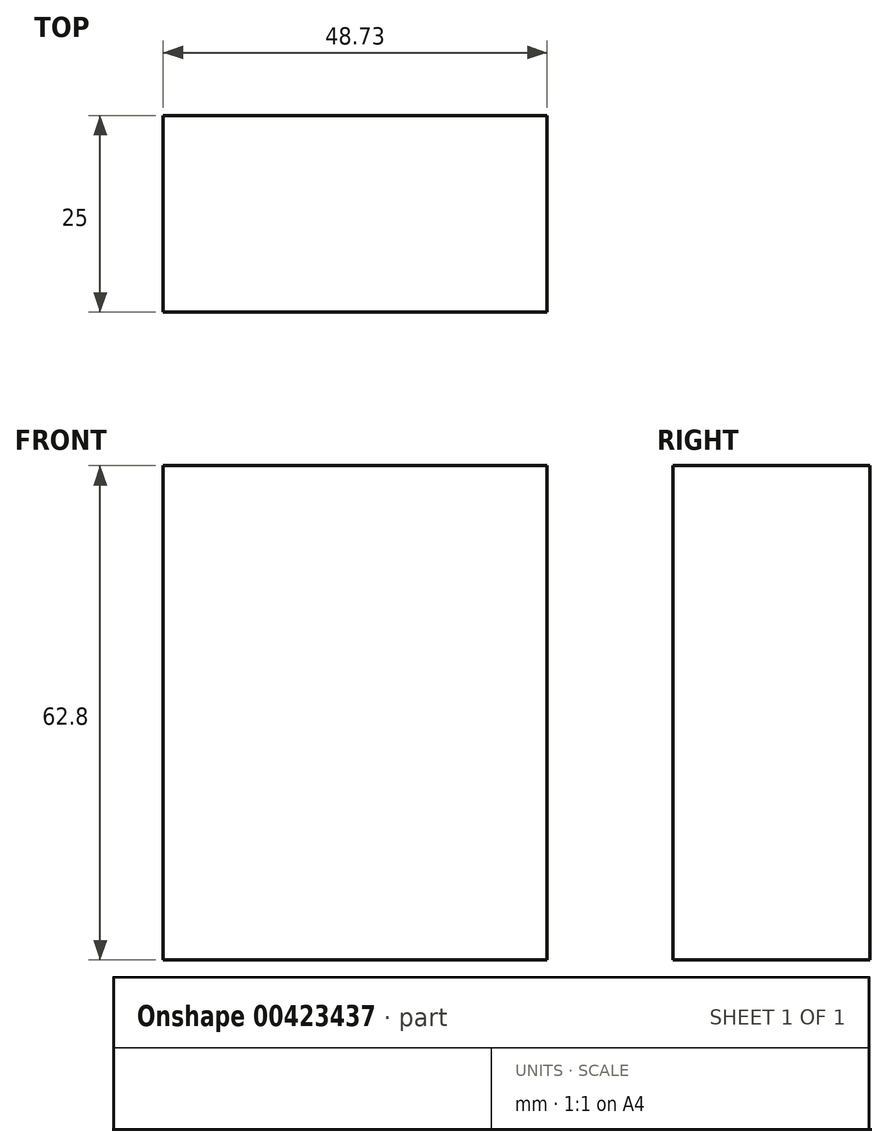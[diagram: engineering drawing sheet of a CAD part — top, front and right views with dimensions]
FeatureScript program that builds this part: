
annotation { "Feature Type Name" : "Feature", "Feature Type Description" : "" }
export const myFeature = defineFeature(function(context is Context, id is Id, definition is map)
    precondition{}
    {
        {
            var Q0;
            Q0=qCreatedBy(makeId("Front.planeOp"),FACE);
            var sketch = newSketch(context, id + "F0", { "sketchPlane" : qUnion([Q0])});
            skLineSegment(sketch, "E0.bottom", {"start": v(-71.43, -5.93) * mm, "end": v(-22.7, -5.93) * mm});
            skLineSegment(sketch, "E0.top", {"start": v(-71.43, 56.87) * mm, "end": v(-22.7, 56.87) * mm});
            skLineSegment(sketch, "E0.left", {"start": v(-71.43, -5.93) * mm, "end": v(-71.43, 56.87) * mm});
            skLineSegment(sketch, "E0.right", {"start": v(-22.7, -5.93) * mm, "end": v(-22.7, 56.87) * mm});
            skPoint(sketch, "E0.middle", {"position": v(-47.06, 25.47) * mm});
            skSolve(sketch);
        }
        {
            var Q0;
            Q0=makeQuery(id+"F0.imprint","IMPRINT",FACE,{"disambiguationData":[TD([[makeQuery(id+"F0.imprint","IMPRINT",EDGE,{"derivedFrom":sQuery(id+"F0.wireOp",EDGE,"E0.bottom")}),1.0]])]});
            extrude(context, id + "F1", {"entities" : qUnion([Q0]), "depth" : 25 * mm});
        }
    });
